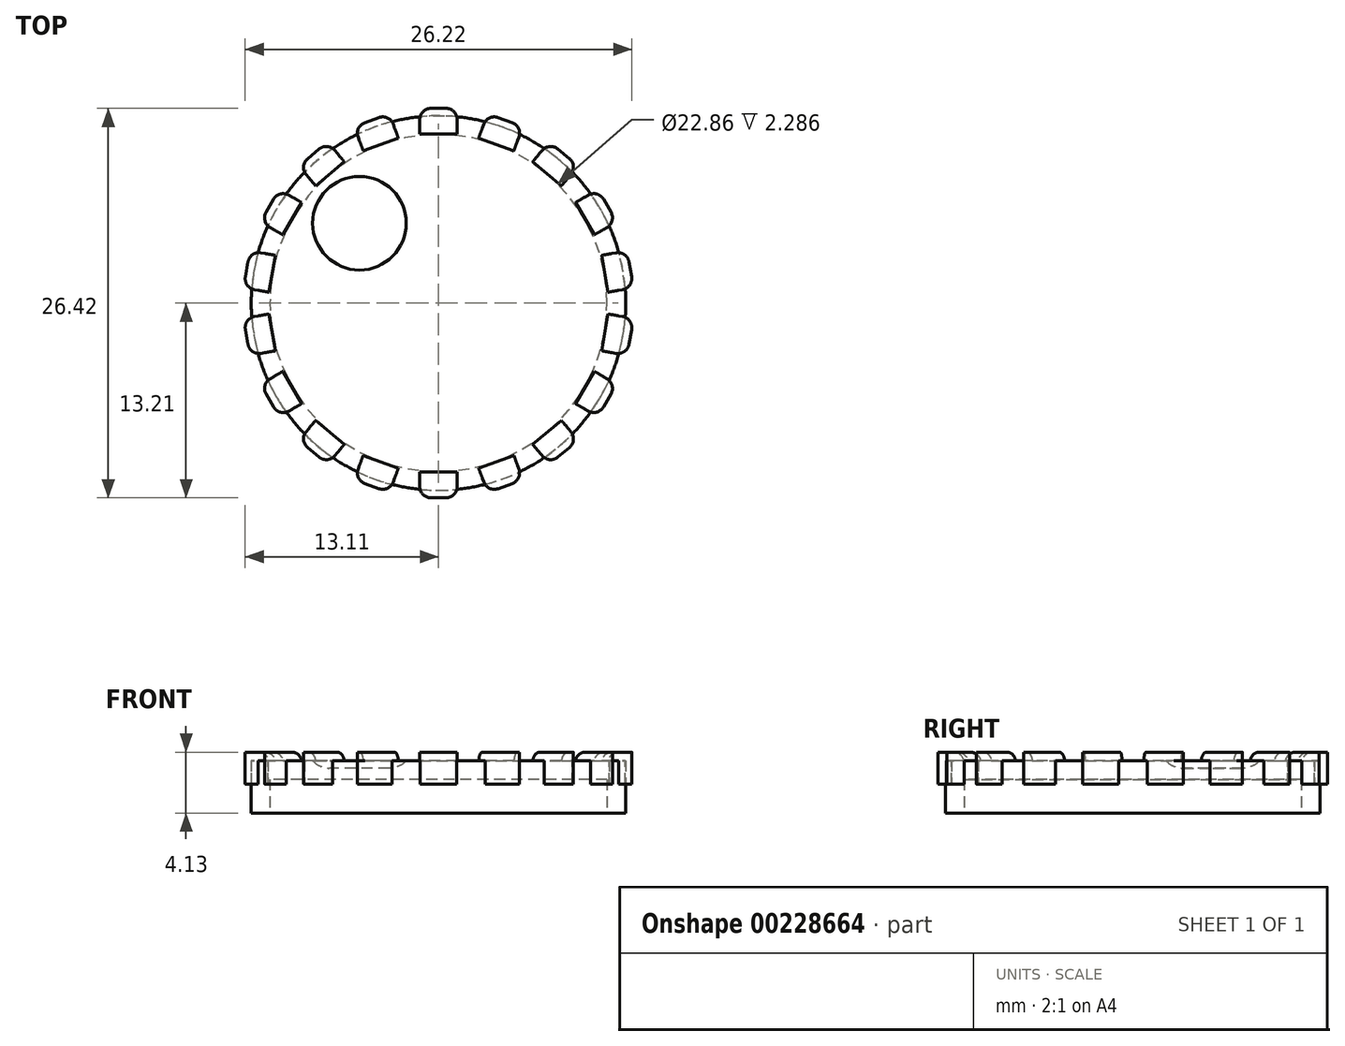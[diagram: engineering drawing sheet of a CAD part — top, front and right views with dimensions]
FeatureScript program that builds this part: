
annotation { "Feature Type Name" : "Feature", "Feature Type Description" : "" }
export const myFeature = defineFeature(function(context is Context, id is Id, definition is map)
    precondition{}
    {
        {
            var Q0;
            Q0=qCreatedBy(makeId("Top.planeOp"),FACE);
            var sketch = newSketch(context, id + "F0", { "sketchPlane" : qUnion([Q0])});
            skCircle(sketch, "E0", {"center": v(0, 0) * mm, "radius": 12.7 * mm});
            skSolve(sketch);
        }
        {
            var Q0;
            Q0 = qSketchRegion(id + "F0", true);
            extrude(context, id + "F1", {"entities" : qUnion([Q0]), "depth" : 3.56 * mm});
        }
        {
            var Q0;
            Q0=makeQuery(id+"F1.opExtrude","CAP_FACE",FACE,{"disambiguationData":[OSD([sQuery(id+"F0.wireOp",EDGE,"E0")])],"isStart":true});
            shell(context, id + "F2", {"entities" : qUnion([Q0]), "thickness" : 1.27 * mm});
        }
        {
            var Q0;
            Q0=makeQuery(id+"F1.opExtrude","CAP_FACE",FACE,{"disambiguationData":[OSD([sQuery(id+"F0.wireOp",EDGE,"E0")])],"isStart":false});
            var sketch = newSketch(context, id + "F3", { "sketchPlane" : qUnion([Q0])});
            skCircle(sketch, "E1", {"center": v(-5.36, 5.42) * mm, "radius": 3.18 * mm});
            skSolve(sketch);
        }
        {
            var Q0;
            Q0=makeQuery(id+"F3.imprint","IMPRINT",FACE,{"disambiguationData":[TD([[makeQuery(id+"F3.imprint","IMPRINT",EDGE,{"derivedFrom":sQuery(id+"F3.wireOp",EDGE,"E1")}),1.0]])]});
            extrude(context, id + "F4", {"entities" : qUnion([Q0]), "operationType" : NewBodyOperationType.REMOVE, "oppositeDirection" : true, "depth" : 0.5 * mm});
        }
        {
            var Q0;
            Q0=qCreatedBy(makeId("Front.planeOp"),FACE);
            var sketch = newSketch(context, id + "F5", { "sketchPlane" : qUnion([Q0])});
            skLineSegment(sketch, "E2", {"start": v(0, -5.96) * mm, "end": v(0, 12.06) * mm, "construction": true});
            skLineSegment(sketch, "E3.bottom", {"start": v(1.27, 1.97) * mm, "end": v(-1.27, 1.97) * mm});
            skLineSegment(sketch, "E3.top", {"start": v(1.27, 4.13) * mm, "end": v(-1.27, 4.13) * mm});
            skLineSegment(sketch, "E3.left", {"start": v(1.27, 1.97) * mm, "end": v(1.27, 4.13) * mm});
            skLineSegment(sketch, "E3.right", {"start": v(-1.27, 1.97) * mm, "end": v(-1.27, 4.13) * mm});
            skSolve(sketch);
        }
        {
            var Q0;
            Q0=makeQuery(id+"F5.imprint","IMPRINT",FACE,{"disambiguationData":[TD([[makeQuery(id+"F5.imprint","IMPRINT",EDGE,{"derivedFrom":sQuery(id+"F5.wireOp",EDGE,"E3.bottom")}),-1.0]])]});
            extrude(context, id + "F6", {"entities" : qUnion([Q0]), "depth" : 13.2 * mm, "hasSecondDirection" : true, "secondDirectionOppositeDirection" : false, "secondDirectionDepth" : 11.43 * mm});
        }
        {
            var Q0;
            Q0=makeQuery(id+"F6.opExtrude","CAP_EDGE",EDGE,{"disambiguationData":[OSD([sQuery(id+"F5.wireOp",EDGE,"E3.right")])],"isStart":false});
            var Q1;
            Q1=makeQuery(id+"F6.opExtrude","CAP_EDGE",EDGE,{"disambiguationData":[OSD([sQuery(id+"F5.wireOp",EDGE,"E3.left")])],"isStart":false});
            var Q2;
            Q2=makeQuery(id+"F6.opExtrude","CAP_EDGE",EDGE,{"disambiguationData":[OSD([sQuery(id+"F5.wireOp",EDGE,"E3.top")])],"isStart":true});
            fillet(context, id + "F7", {"entities" : qUnion([Q0, Q1, Q2]), "radius" : 0.76 * mm, "tangentPropagation" : true, "allowEdgeOverflow" : false});
        }
        {
            var Q0;
            Q0=makeQuery(id+"F6.opExtrude","SWEPT_BODY",BODY,{"disambiguationData":[OSD([sQuery(id+"F5.wireOp",EDGE,"E3.bottom"),sQuery(id+"F5.wireOp",EDGE,"E3.top"),sQuery(id+"F5.wireOp",EDGE,"E3.left"),sQuery(id+"F5.wireOp",EDGE,"E3.right")])]});
            var Q1;
            Q1=sQuery(id+"F5.wireOp",EDGE,"E2");
            circularPattern(context, id + "F8", {"operationType" : NewBodyOperationType.ADD, "entities" : qUnion([Q0]), "axis" : qUnion([Q1]), "angle" : 360 * degree, "instanceCount" : 18, "equalSpace" : true});
        }
        {
            var Q0;
            Q0=makeQuery(id+"F4.boolean.opBoolean","COPY",EDGE,{"derivedFrom":makeQuery(id+"F4.opExtrude","CAP_EDGE",EDGE,{"disambiguationData":[OSD([sQuery(id+"F3.wireOp",EDGE,"E1")])],"isStart":false})});
            fillet(context, id + "F9", {"entities" : qUnion([Q0]), "radius" : 1.52 * mm, "allowEdgeOverflow" : false});
        }
    });
